# Revit family: 35_751250001_Valvula Push de Empotrar Taza
name_source: partatom
category: Aparatos sanitarios
revit_build: Autodesk Revit 2018 (Build: 20170223_1515(x64)
units: mm (PartAtom-declared; Revit-internal decimal feet)

## family parameters
Anfitrión = Muro
Compartido = No
Corte con vacíos al cargar = No
Cota de conector redondo = Diámetro de uso
Número OmniClass = 23.45.05.21.11.11
Punto de cálculo de habitación = No
Siempre vertical = Sí
Tipo de pieza = Normal
Título OmniClass = Water Operated Water Closets

## types (1)
- Tipo 1
    Accionamiento = Push
    Consumo de Agua = 4.8 Litros por descarga
    Cumple EDGE = SI
    Cumple LEED = SI
    Diametro conexión = 1-1/4" 11,5 NSPM
    Garantía = 3 años
    Marca = CORONA
    Nombre = Valvula Push de Empotrar Taza
    Presión Máxima = 80 PSI
    Presión Mínima = 35 PSI
    Referencia = 751250001
    Tipo = Válvula descarga
    Tráfico = Institucional Alto tráfico
    URL = https://www.corona.co
    Vida Util (ciclos) = 150000
